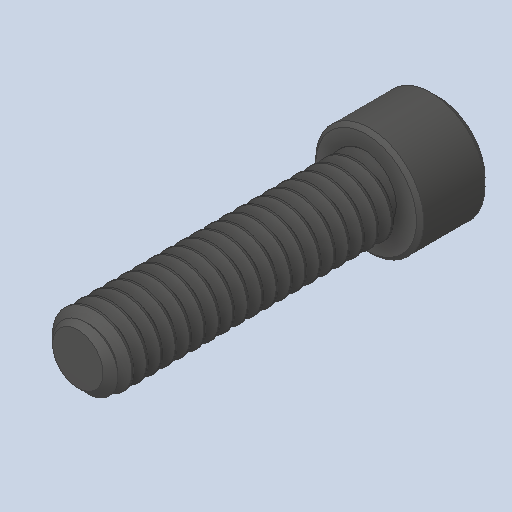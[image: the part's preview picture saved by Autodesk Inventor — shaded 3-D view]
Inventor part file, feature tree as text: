
AUTODESK INVENTOR PART (.ipt)
format: ipt  version: 2023.4 (Build 274418000, 418)  size: 705,536 bytes
history: native  units: in
note: dims shown in document units (in); Inventor stores cm internally (conversion verified against a paired STEP export)
features: chamfer x1
ambient origin geometry x8: Origin, YZ Plane, XZ Plane, XY Plane, X Axis, Y Axis, Z Axis, Center Point
bodies: Solid1 (feature_tree)
feature tree (1):
  chamfer  "Chamfer2"  [1 undecoded]
note: 1 required parameter value undecoded (feature->parameter linkage not recoverable at this tier; creation-order binding heuristic only, values carry confidence <= 0.55)
